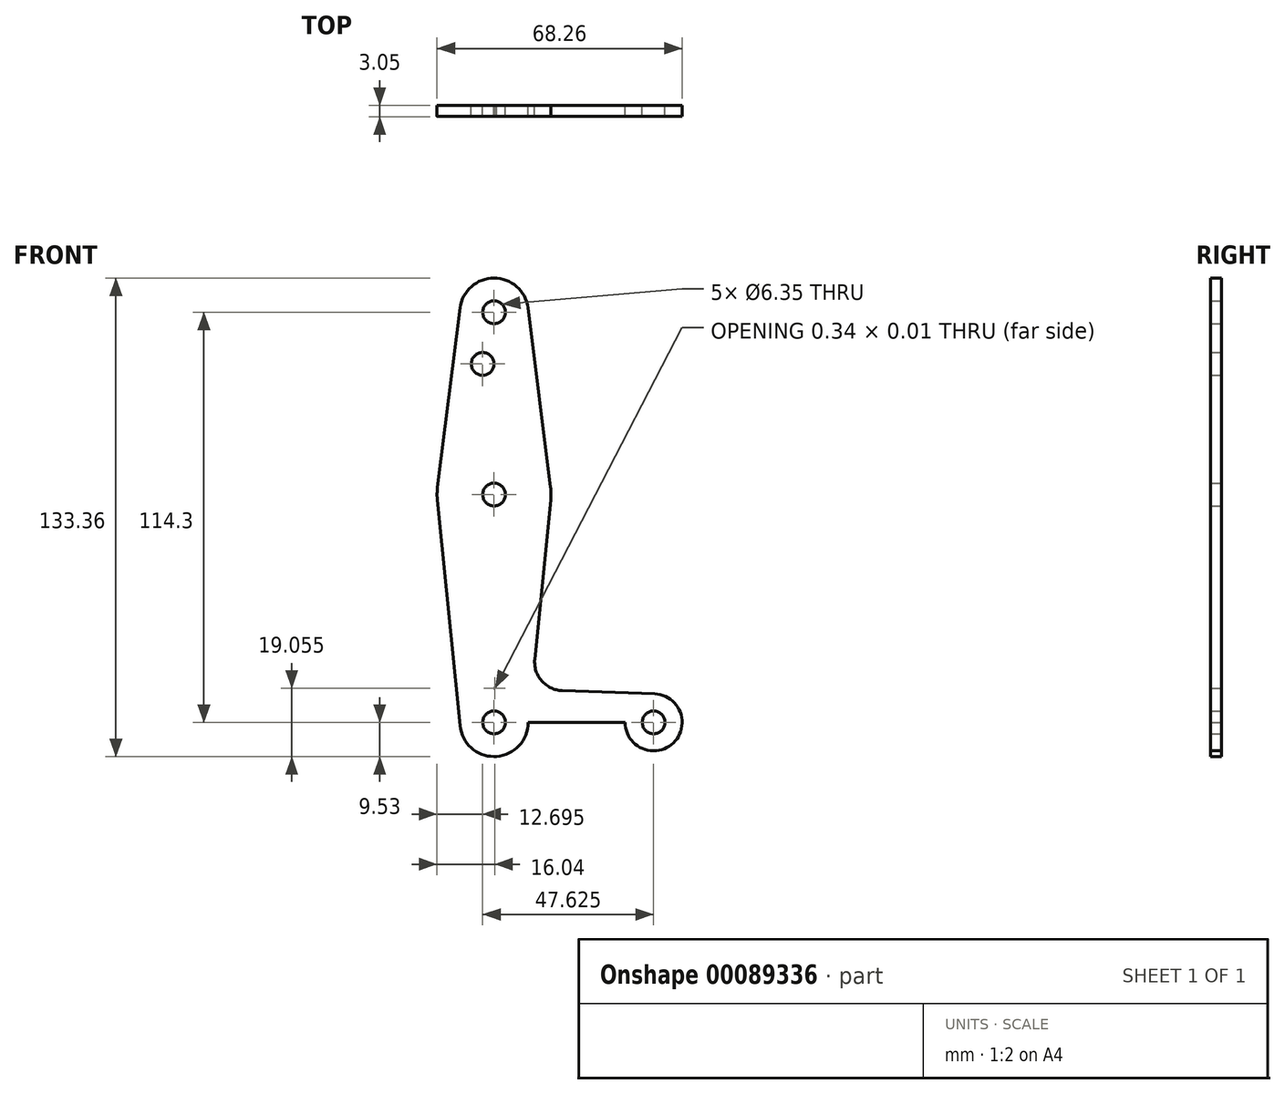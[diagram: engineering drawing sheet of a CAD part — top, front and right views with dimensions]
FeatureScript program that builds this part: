
annotation { "Feature Type Name" : "Feature", "Feature Type Description" : "" }
export const myFeature = defineFeature(function(context is Context, id is Id, definition is map)
    precondition{}
    {
        {
            var Q0;
            Q0=qCreatedBy(makeId("Front.planeOp"),FACE);
            var sketch = newSketch(context, id + "F0", { "sketchPlane" : qUnion([Q0])});
            skCircle(sketch, "E0", {"center": v(0, 114.3) * mm, "radius": 9.53 * mm});
            skCircle(sketch, "E1", {"center": v(0, 63.5) * mm, "radius": 15.88 * mm});
            skCircle(sketch, "E2", {"center": v(0, 0) * mm, "radius": 9.53 * mm});
            skCircle(sketch, "E3", {"center": v(44.45, 0) * mm, "radius": 7.94 * mm});
            skLineSegment(sketch, "E4", {"start": v(0, 114.3) * mm, "end": v(0, 0) * mm});
            skLineSegment(sketch, "E5", {"start": v(0, 0) * mm, "end": v(44.45, 0) * mm});
            skLineSegment(sketch, "E6", {"start": v(-15.8, 61.91) * mm, "end": v(-9.48, -0.95) * mm});
            skLineSegment(sketch, "E7", {"start": v(15.8, 61.91) * mm, "end": v(11.34, 17.6) * mm});
            skLineSegment(sketch, "E8", {"start": v(18.97, 8.85) * mm, "end": v(44.73, 7.93) * mm});
            skLineSegment(sketch, "E9", {"start": v(0, -9.53) * mm, "end": v(44.73, -7.93) * mm});
            skLineSegment(sketch, "E10", {"start": v(9.45, 115.5) * mm, "end": v(15.75, 65.48) * mm});
            skLineSegment(sketch, "E11", {"start": v(-9.45, 115.5) * mm, "end": v(-15.75, 65.48) * mm});
            skCircle(sketch, "E12", {"center": v(0, 63.5) * mm, "radius": 3.18 * mm});
            skCircle(sketch, "E13", {"center": v(0, 0) * mm, "radius": 3.18 * mm});
            skCircle(sketch, "E14", {"center": v(44.45, 0) * mm, "radius": 3.18 * mm});
            skCircle(sketch, "E15", {"center": v(0, 114.3) * mm, "radius": 3.18 * mm});
            skPoint(sketch, "E16.newPointA", {"position": v(9.57, 0) * mm});
            skPoint(sketch, "E16.newPointB", {"position": v(0, 9.53) * mm});
            skArc(sketch, "E16.filletArc", {"start": v(11.34, 17.6) * mm, "mid": v(13.26, 11.57) * mm, "end": v(18.97, 8.85) * mm});
            skLineSegment(sketch, "E17", {"start": v(18.97, 8.85) * mm, "end": v(0, 9.53) * mm});
            skLineSegment(sketch, "E18", {"start": v(11.34, 17.6) * mm, "end": v(9.57, 0) * mm});
            skCircle(sketch, "E19", {"center": v(-3.17, 99.9) * mm, "radius": 3.18 * mm});
            skSolve(sketch);
        }
        {
            var Q0;
            {var subQ0=sQuery(id+"F0.wireOp",EDGE,"E9");var subQ1=sQuery(id+"F0.wireOp",EDGE,"E2");var subQ2=makeQuery(id+"F0.imprint","INTERSECT",VERTEX,{"disambiguationData":[OD(0.0)],"derivedFrom":[subQ1,subQ0]});Q0=makeQuery(id+"F0.imprint","IMPRINT",FACE,{"disambiguationData":[TD([[makeQuery(id+"F0.imprint","IMPRINT",EDGE,{"disambiguationData":[TD([[subQ2,-1.0]])],"derivedFrom":subQ1}),1.0]])]});}
            var Q1;
            {var subQ0=sQuery(id+"F0.wireOp",EDGE,"E16.filletArc");Q1=makeQuery(id+"F0.imprint","IMPRINT",FACE,{"disambiguationData":[TD([[makeQuery(id+"F0.imprint","IMPRINT",EDGE,{"derivedFrom":subQ0}),-1.0]])]});}
            var Q2;
            Q2=makeQuery(id+"F0.imprint","IMPRINT",FACE,{"disambiguationData":[TD([[makeQuery(id+"F0.imprint","IMPRINT",EDGE,{"derivedFrom":sQuery(id+"F0.wireOp",EDGE,"E15")}),-1.0]])]});
            var Q3;
            {var subQ6=sQuery(id+"F0.wireOp",EDGE,"E10");Q3=makeQuery(id+"F0.imprint","IMPRINT",FACE,{"disambiguationData":[TD([[makeQuery(id+"F0.imprint","IMPRINT",EDGE,{"derivedFrom":subQ6}),-1.0]])]});}
            var Q4;
            Q4=makeQuery(id+"F0.imprint","IMPRINT",FACE,{"disambiguationData":[TD([[makeQuery(id+"F0.imprint","IMPRINT",EDGE,{"derivedFrom":sQuery(id+"F0.wireOp",EDGE,"E14")}),-1.0]])]});
            var Q5;
            {var subQ5=sQuery(id+"F0.wireOp",EDGE,"E11");Q5=makeQuery(id+"F0.imprint","IMPRINT",FACE,{"disambiguationData":[TD([[makeQuery(id+"F0.imprint","IMPRINT",EDGE,{"derivedFrom":subQ5}),1.0]])]});}
            var Q6;
            {var subQ0=sQuery(id+"F0.wireOp",EDGE,"E1");var subQ2=makeQuery(id+"F0.imprint","INTERSECT",VERTEX,{"derivedFrom":[subQ0,sQuery(id+"F0.wireOp",EDGE,"E10")]});Q6=makeQuery(id+"F0.imprint","IMPRINT",FACE,{"disambiguationData":[TD([[makeQuery(id+"F0.imprint","IMPRINT",EDGE,{"disambiguationData":[TD([[subQ2,-1.0]])],"derivedFrom":subQ0}),1.0]])]});}
            var Q7;
            {var subQ1=sQuery(id+"F0.wireOp",EDGE,"E1");var subQ8=makeQuery(id+"F0.imprint","INTERSECT",VERTEX,{"derivedFrom":[subQ1,sQuery(id+"F0.wireOp",EDGE,"E11")]});Q7=makeQuery(id+"F0.imprint","IMPRINT",FACE,{"disambiguationData":[TD([[makeQuery(id+"F0.imprint","IMPRINT",EDGE,{"disambiguationData":[TD([[subQ8,1.0]])],"derivedFrom":subQ1}),1.0]])]});}
            var Q8;
            {var subQ6=sQuery(id+"F0.wireOp",EDGE,"E6");Q8=makeQuery(id+"F0.imprint","IMPRINT",FACE,{"disambiguationData":[TD([[makeQuery(id+"F0.imprint","IMPRINT",EDGE,{"derivedFrom":subQ6}),1.0]])]});}
            var Q9;
            {var subQ0=sQuery(id+"F0.wireOp",EDGE,"E9");var subQ6=sQuery(id+"F0.wireOp",EDGE,"E2");var subQ8=makeQuery(id+"F0.imprint","INTERSECT",VERTEX,{"disambiguationData":[OD(1.0)],"derivedFrom":[subQ6,subQ0]});Q9=makeQuery(id+"F0.imprint","IMPRINT",FACE,{"disambiguationData":[TD([[makeQuery(id+"F0.imprint","IMPRINT",EDGE,{"disambiguationData":[TD([[subQ8,-1.0]])],"derivedFrom":subQ6}),-1.0]])]});}
            var Q10;
            {var subQ0=sQuery(id+"F0.wireOp",EDGE,"E8");Q10=makeQuery(id+"F0.imprint","IMPRINT",FACE,{"disambiguationData":[TD([[makeQuery(id+"F0.imprint","IMPRINT",EDGE,{"derivedFrom":subQ0}),-1.0]])]});}
            var Q11;
            {var subQ4=sQuery(id+"F0.wireOp",EDGE,"E7");Q11=makeQuery(id+"F0.imprint","IMPRINT",FACE,{"disambiguationData":[TD([[makeQuery(id+"F0.imprint","IMPRINT",EDGE,{"derivedFrom":subQ4}),-1.0]])]});}
            var Q12;
            {var subQ1=sQuery(id+"F0.wireOp",EDGE,"E2");var subQ9=makeQuery(id+"F0.imprint","INTERSECT",VERTEX,{"derivedFrom":[subQ1,sQuery(id+"F0.wireOp",EDGE,"E6")]});Q12=makeQuery(id+"F0.imprint","IMPRINT",FACE,{"disambiguationData":[TD([[makeQuery(id+"F0.imprint","IMPRINT",EDGE,{"disambiguationData":[TD([[subQ9,1.0]])],"derivedFrom":subQ1}),1.0]])]});}
            var Q13;
            {var subQ1=sQuery(id+"F0.wireOp",EDGE,"E2");var subQ8=makeQuery(id+"F0.imprint","INTERSECT",VERTEX,{"derivedFrom":[subQ1,sQuery(id+"F0.wireOp",EDGE,"E17")]});Q13=makeQuery(id+"F0.imprint","IMPRINT",FACE,{"disambiguationData":[TD([[makeQuery(id+"F0.imprint","IMPRINT",EDGE,{"disambiguationData":[TD([[subQ8,1.0]])],"derivedFrom":subQ1}),1.0]])]});}
            var Q14;
            {var subQ0=sQuery(id+"F0.wireOp",EDGE,"E17");var subQ1=sQuery(id+"F0.wireOp",EDGE,"E2");var subQ2=makeQuery(id+"F0.imprint","INTERSECT",VERTEX,{"derivedFrom":[subQ1,subQ0]});Q14=makeQuery(id+"F0.imprint","IMPRINT",FACE,{"disambiguationData":[TD([[makeQuery(id+"F0.imprint","IMPRINT",EDGE,{"disambiguationData":[TD([[subQ2,1.0]])],"derivedFrom":subQ1}),-1.0]])]});}
            extrude(context, id + "F1", {"entities" : qUnion([Q0, Q1, Q2, Q3, Q4, Q5, Q6, Q7, Q8, Q9, Q10, Q11, Q12, Q13, Q14]), "depth" : 3.05 * mm});
        }
    });
